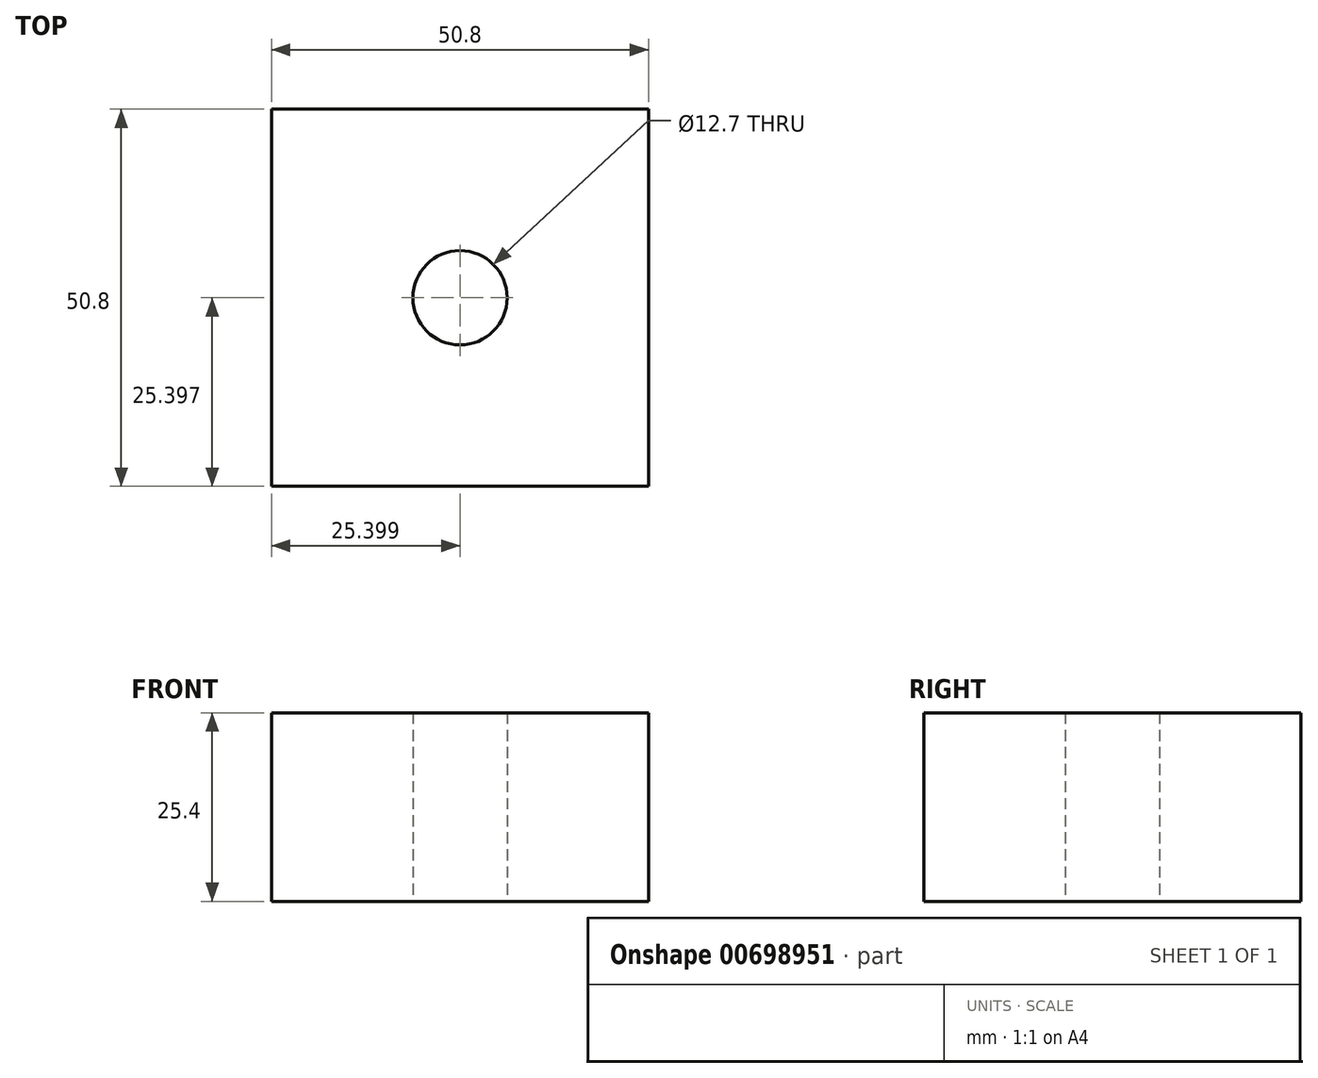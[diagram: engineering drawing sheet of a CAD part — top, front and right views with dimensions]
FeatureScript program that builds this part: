
annotation { "Feature Type Name" : "Feature", "Feature Type Description" : "" }
export const myFeature = defineFeature(function(context is Context, id is Id, definition is map)
    precondition{}
    {
        {
            var Q0;
            Q0=qCreatedBy(makeId("Top.planeOp"),FACE);
            var sketch = newSketch(context, id + "F0", { "sketchPlane" : qUnion([Q0])});
            skLineSegment(sketch, "E0", {"start": v(58.07, -32.57) * mm, "end": v(7.27, -32.57) * mm});
            skLineSegment(sketch, "E1", {"start": v(58.07, 18.23) * mm, "end": v(58.07, -32.57) * mm});
            skLineSegment(sketch, "E2", {"start": v(7.27, -32.57) * mm, "end": v(7.27, 18.23) * mm});
            skLineSegment(sketch, "E3", {"start": v(7.27, 18.23) * mm, "end": v(58.07, 18.23) * mm});
            skCircle(sketch, "E4", {"center": v(32.67, -7.17) * mm, "radius": 6.35 * mm});
            skSolve(sketch);
        }
        {
            var Q0;
            Q0=makeQuery(id+"F0.imprint","IMPRINT",FACE,{"disambiguationData":[TD([[makeQuery(id+"F0.imprint","IMPRINT",EDGE,{"derivedFrom":sQuery(id+"F0.wireOp",EDGE,"E0")}),-1.0]])]});
            extrude(context, id + "F1", {"entities" : qUnion([Q0]), "depth" : 25.4 * mm, "offsetDistance" : 25.4 * mm});
        }
    });
